# Revit family: Hager-Univers-IP55-D400-H2050-Cl.II-Steel_encl-NoHosted-ES-es
name_source: partatom
category: Electrical Equipment
units: mm (PartAtom-declared; Revit-internal decimal feet)

## family parameters
Always vertical = Yes
Cut with Voids When Loaded = No
Panel Configuration = Two Columns, Circuits Across
Part Type = Panelboard
Room Calculation Point = No
Round Connector Dimension = Use Diameter
Shared = No
Work Plane-Based = Yes

## types (11) — shared parameters
Default Elevation = 1219 mm
EF000003 - Tipo de montaje = EV012274 - Instalación de suelo
EF000007 - Color = EV000270 - Gris
EF000040 - Altura = 2050 mm  [stored 6.72572 ft]
EF000049 - Profundidad = 400 mm  [stored 1.31234 ft]
EF000116 - Número RAL = 7035
EF000118 - Con placa de montaje = No
EF000266 - Número de filas = 12
EF000339 - Tipo de cubierta = EV004216 - Puerta
EF001088 - Posibilidad de extensión = Yes
EF001131 - Profundidad interna = 400 mm  [stored 1.31234 ft]
EF001596 - Material de la carcasa = EV000179 - Acero
EF001613 - Integridad del circuito = EV000494 - Ninguno
EF002950 - Anchura de unidades de división = 24
EF003532 - Adecuado para uso en exteriores = No
EF004293 - Resistencia al impacto (IK) = EV008784 - IK10
EF005474 - Grado de protección (IP) = EV006420 - IP55
EF006306 - Con cierre = No
EF007800 - Adecuado para la protección contra rayos = No
EF008873 - Corriente nominal (In) = 800 A
EF009170 - Espesor del material de la caja = 2 mm  [stored 0.00656168 ft]
EF009171 - Espesor puerta/tapa = 2 mm  [stored 0.00656168 ft]
EF009212 - Versión de la cubierta = EV000116 - Cerrado
EF015940 - Tapa con alivio de sobrepresión = No
HG000002 - Con puerta o tapa = Yes
HG000003 - Gama = Univers
HG000006 - Empotrado = No
HG000023 - Caja de doble sección = No
HG000024 - Altura de la sección inferior = 600 mm
HG000026 - Instalación en suelo = Yes
HG000027 - Altura de zócalo = 200 mm  [stored 0.656168 ft]
Manufacturer = Hager
Type Comments = Univers
zero-valued in all types: EF000218 - Profundidad de instalación

## per-type parameters (varying)
| type | EF000008 - Anchura | EF000437 - Número de entradas de conductos de cables | EF004427 - Número de módulos | EF004464 - Tipo de puerta | EF006244 - Tapa/puerta transparente | EF009554 - Número de aberturas para placas-brida | HG000004 - Referencia del fabricante | HG000009 - Puerta batiente doble | HG000010 - Puertas asimétricas |
| Instalación de suelo IP55 A1050 A2050 P400  - FR24H2 | 1050 mm | 8 | 576 | EV003602 - Doble | No | 8 | FR24H2 | Yes | Yes |
| Instalación de suelo IP55 A1050 A2050 P400  - FR24U2 | 1050 mm | 8 | 576 | EV003602 - Doble | Yes | 8 | FR24U2 | Yes | Yes |
| Instalación de suelo IP55 A1300 A2050 P400  - FR25H2 | 1300 mm  [stored 4.26509 ft] | 10 | 720 | EV003602 - Doble | No | 10 | FR25H2 | Yes | Yes |
| Instalación de suelo IP55 A1300 A2050 P400  - FR25U2 | 1300 mm  [stored 4.26509 ft] | 10 | 720 | EV003602 - Doble | Yes | 10 | FR25U2 | Yes | Yes |
| Instalación de suelo IP55 A1550 A2050 P400  - FR26H2 | 1550 mm  [stored 5.0853 ft] | 12 | 864 | EV003602 - Doble | No | 12 | FR26H2 | Yes | Yes |
| Instalación de suelo IP55 A1550 A2050 P400  - FR26U2 | 1550 mm  [stored 5.0853 ft] | 12 | 864 | EV003602 - Doble | Yes | 12 | FR26U2 | Yes | Yes |
| Instalación de suelo IP55 A300 A2050 P400  - FR21H2 | 300 mm | 2 | 144 | EV002646 - Único | No | 2 | FR21H2 | No | No |
| Instalación de suelo IP55 A550 A2050 P400  - FR22H2 | 550 mm | 4 | 288 | EV002646 - Único | No | 4 | FR22H2 | No | No |
| Instalación de suelo IP55 A550 A2050 P400  - FR22U2 | 550 mm | 4 | 288 | EV002646 - Único | Yes | 4 | FR22U2 | No | No |
| Instalación de suelo IP55 A800 A2050 P400  - FR23H2 | 800 mm  [stored 2.62467 ft] | 6 | 432 | EV002646 - Único | No | 6 | FR23H2 | No | No |
| Instalación de suelo IP55 A800 A2050 P400  - FR23U2 | 800 mm  [stored 2.62467 ft] | 6 | 432 | EV002646 - Único | Yes | 6 | FR23U2 | No | No |

note: [stored X ft] marks values corroborated as IEEE doubles in the binary element streams (Revit-internal decimal feet)

## geometry (parser evidence)
native form markers: Blend x4, Sweep x11
no freeform markers — native parametric forms only
